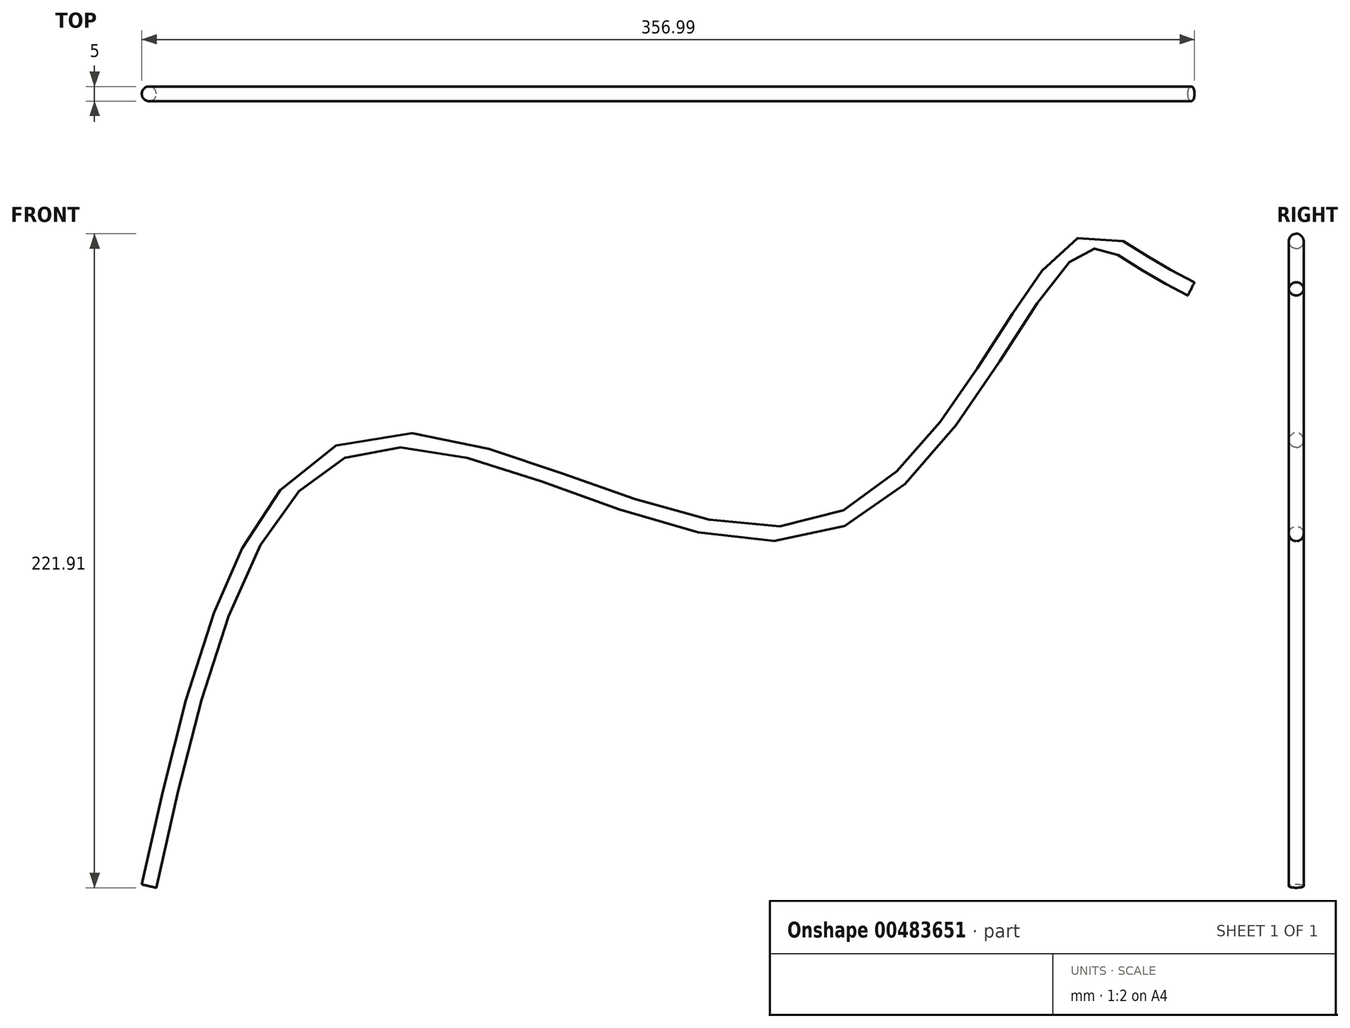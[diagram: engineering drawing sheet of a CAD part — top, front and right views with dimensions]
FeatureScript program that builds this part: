
annotation { "Feature Type Name" : "Feature", "Feature Type Description" : "" }
export const myFeature = defineFeature(function(context is Context, id is Id, definition is map)
    precondition{}
    {
        {
            var Q0;
            Q0=qCreatedBy(makeId("Front.planeOp"),FACE);
            var sketch = newSketch(context, id + "F0", { "sketchPlane" : qUnion([Q0])});
            skFitSpline(sketch, "E0", {"points": [v(-159.4, -82.65) * mm, v(-84.58, 67.95) * mm, v(71, 40.06) * mm, v(155.48, 134.45) * mm, v(177.16, 129.41) * mm, v(194, 120.03) * mm], "startDerivative": vector(168, 757.22) * mm, "endDerivative": vector(169.75, -86.18) * mm});
            skSolve(sketch);
        }
        {
            var Q0;
            Q0=sQuery(id+"F0.wireOp",VERTEX,"E0.start");
            var Q1;
            Q1=sQuery(id+"F0.wireOp",EDGE,"E0");
            cPlane(context, id + "F1", {"entities" : qUnion([Q0, Q1]), "cplaneType" : CPlaneType.CURVE_POINT, "offset" : 25 * mm, "width" : 150 * mm, "height" : 150 * mm});
        }
        {
            var Q0;
            Q0=qCreatedBy(id+"F1.planeOp",FACE);
            var sketch = newSketch(context, id + "F2", { "sketchPlane" : qUnion([Q0])});
            skCircle(sketch, "E1", {"center": v(-137.73, 0) * mm, "radius": 2.5 * mm});
            skSolve(sketch);
        }
        {
            var Q0;
            Q0=makeQuery(id+"F2.imprint","IMPRINT",FACE,{"disambiguationData":[TD([[makeQuery(id+"F2.imprint","IMPRINT",EDGE,{"derivedFrom":sQuery(id+"F2.wireOp",EDGE,"E1")}),1.0]])]});
            var Q1;
            Q1=sQuery(id+"F0.wireOp",EDGE,"E0");
            sweep(context, id + "F3", {"profiles" : qUnion([Q0]), "path" : qUnion([Q1])});
        }
    });
